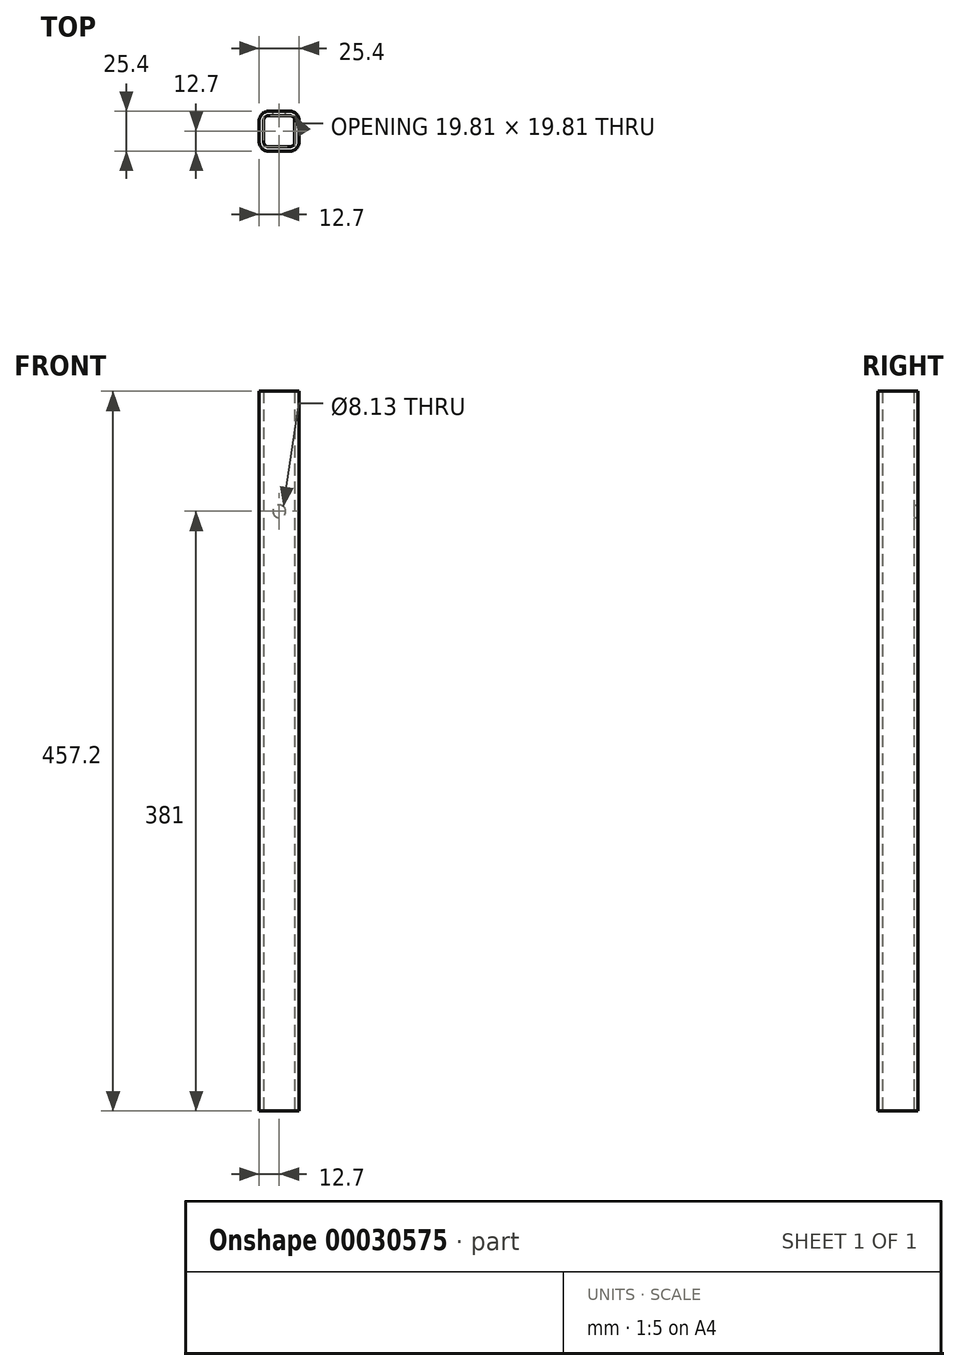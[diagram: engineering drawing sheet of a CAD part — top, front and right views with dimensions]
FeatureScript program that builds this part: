
annotation { "Feature Type Name" : "Feature", "Feature Type Description" : "" }
export const myFeature = defineFeature(function(context is Context, id is Id, definition is map)
    precondition{}
    {
        {
            var Q0;
            Q0=qCreatedBy(makeId("Top.planeOp"),FACE);
            var sketch = newSketch(context, id + "F0", { "sketchPlane" : qUnion([Q0])});
            skLineSegment(sketch, "E0.bottom", {"start": v(5.97, 0) * mm, "end": v(19.43, 0) * mm});
            skLineSegment(sketch, "E0.top", {"start": v(5.97, 25.4) * mm, "end": v(19.43, 25.4) * mm});
            skLineSegment(sketch, "E0.left", {"start": v(0, 5.97) * mm, "end": v(0, 19.43) * mm});
            skLineSegment(sketch, "E0.right", {"start": v(25.4, 5.97) * mm, "end": v(25.4, 19.43) * mm});
            skLineSegment(sketch, "E1.0", {"start": v(5.97, 22.6) * mm, "end": v(19.43, 22.6) * mm});
            skLineSegment(sketch, "E1.1", {"start": v(2.8, 5.97) * mm, "end": v(2.8, 19.43) * mm});
            skLineSegment(sketch, "E1.2", {"start": v(5.97, 2.8) * mm, "end": v(19.43, 2.8) * mm});
            skLineSegment(sketch, "E1.3", {"start": v(22.6, 5.97) * mm, "end": v(22.6, 19.43) * mm});
            skPoint(sketch, "E2.visualSharp", {"position": v(2.8, 22.6) * mm});
            skArc(sketch, "E2.filletArc", {"start": v(5.97, 22.6) * mm, "mid": v(3.72, 21.68) * mm, "end": v(2.8, 19.43) * mm});
            skPoint(sketch, "E3.visualSharp", {"position": v(22.6, 22.6) * mm});
            skArc(sketch, "E3.filletArc", {"start": v(22.6, 19.43) * mm, "mid": v(21.68, 21.68) * mm, "end": v(19.43, 22.6) * mm});
            skPoint(sketch, "E4.visualSharp", {"position": v(22.6, 2.8) * mm});
            skArc(sketch, "E4.filletArc", {"start": v(19.43, 2.8) * mm, "mid": v(21.68, 3.72) * mm, "end": v(22.6, 5.97) * mm});
            skPoint(sketch, "E5.visualSharp", {"position": v(2.8, 2.8) * mm});
            skArc(sketch, "E5.filletArc", {"start": v(2.8, 5.97) * mm, "mid": v(3.72, 3.72) * mm, "end": v(5.97, 2.8) * mm});
            skPoint(sketch, "E6.visualSharp", {"position": v(0, 25.4) * mm});
            skArc(sketch, "E6.filletArc", {"start": v(5.97, 25.4) * mm, "mid": v(1.75, 23.65) * mm, "end": v(0, 19.43) * mm});
            skPoint(sketch, "E7.visualSharp", {"position": v(25.4, 25.4) * mm});
            skArc(sketch, "E7.filletArc", {"start": v(25.4, 19.43) * mm, "mid": v(23.65, 23.65) * mm, "end": v(19.43, 25.4) * mm});
            skPoint(sketch, "E8.visualSharp", {"position": v(25.4, 0) * mm});
            skArc(sketch, "E8.filletArc", {"start": v(19.43, 0) * mm, "mid": v(23.65, 1.75) * mm, "end": v(25.4, 5.97) * mm});
            skPoint(sketch, "E9.visualSharp", {"position": v(0, 0) * mm});
            skArc(sketch, "E9.filletArc", {"start": v(0, 5.97) * mm, "mid": v(1.75, 1.75) * mm, "end": v(5.97, 0) * mm});
            skSolve(sketch);
        }
        {
            var Q0;
            Q0=makeQuery(id+"F0.imprint","IMPRINT",FACE,{"disambiguationData":[TD([[makeQuery(id+"F0.imprint","IMPRINT",EDGE,{"derivedFrom":sQuery(id+"F0.wireOp",EDGE,"E0.bottom")}),1.0]])]});
            extrude(context, id + "F1", {"entities" : qUnion([Q0]), "depth" : 457.2 * mm});
        }
        {
            var Q0;
            Q0=makeQuery(id+"F1.opExtrude","SWEPT_FACE",FACE,{"disambiguationData":[OSD([sQuery(id+"F0.wireOp",EDGE,"E0.top")])]});
            var sketch = newSketch(context, id + "F2", { "sketchPlane" : qUnion([Q0])});
            skLineSegment(sketch, "E10", {"start": v(-12.7, 457.2) * mm, "end": v(-12.7, 381) * mm});
            skCircle(sketch, "E11", {"center": v(-12.7, 381) * mm, "radius": 4.06 * mm});
            skSolve(sketch);
        }
        {
            var Q0;
            Q0=makeQuery(id+"F2.imprint","IMPRINT",FACE,{"disambiguationData":[TD([[makeQuery(id+"F2.imprint","IMPRINT",EDGE,{"derivedFrom":sQuery(id+"F2.wireOp",EDGE,"E11")}),1.0]])]});
            extrude(context, id + "F3", {"entities" : qUnion([Q0]), "operationType" : NewBodyOperationType.REMOVE, "endBound" : BoundingType.UP_TO_NEXT, "oppositeDirection" : true, "depth" : 25.4 * mm});
        }
    });
